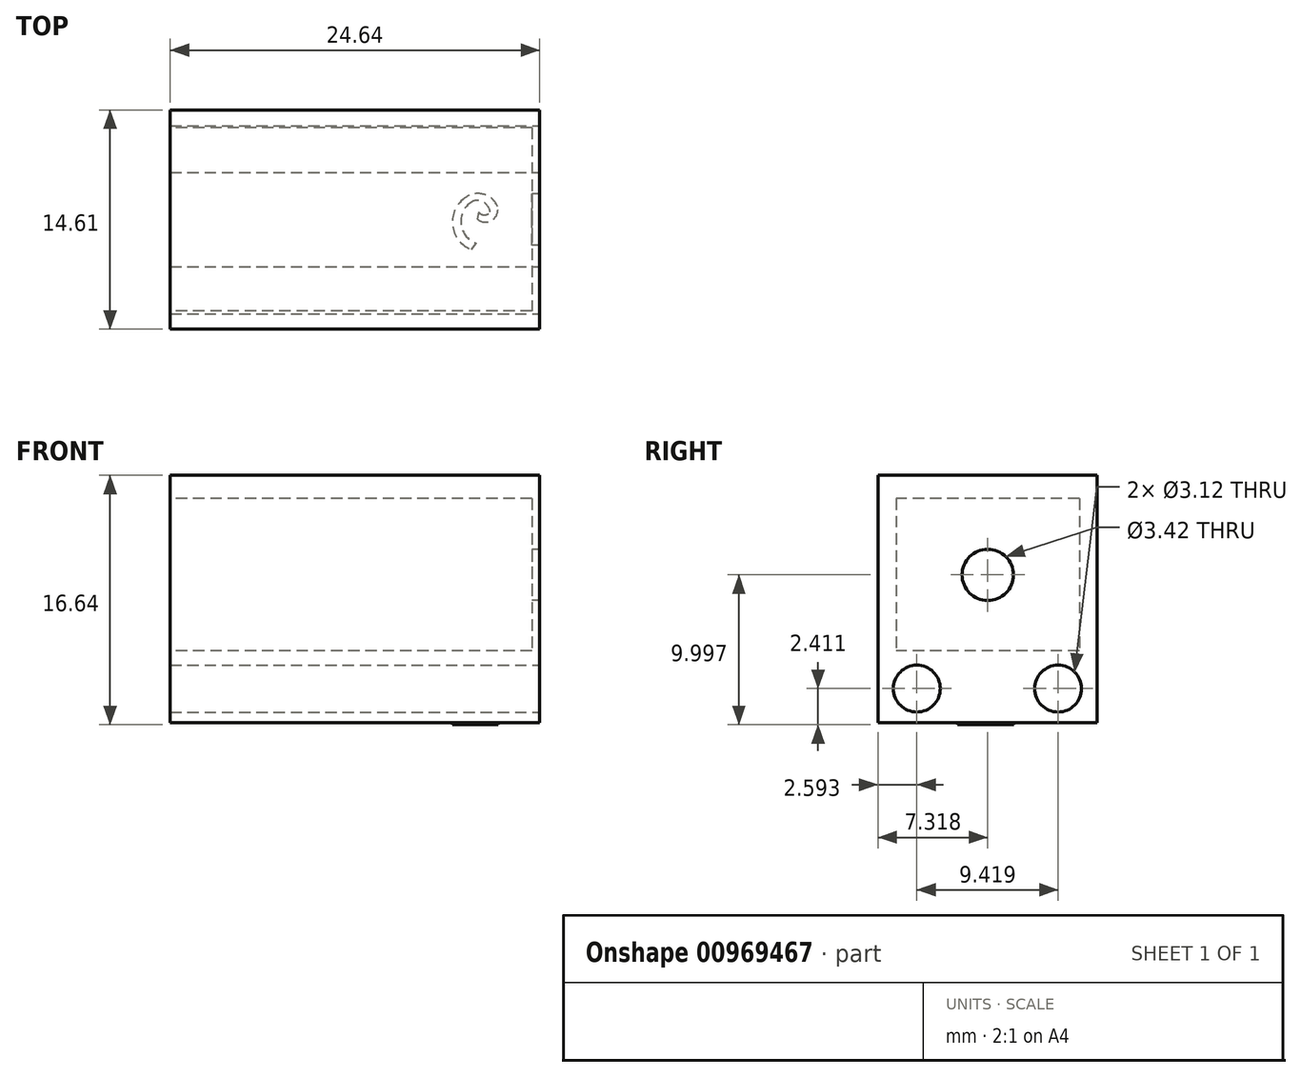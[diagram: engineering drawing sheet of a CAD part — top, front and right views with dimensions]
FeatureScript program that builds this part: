
annotation { "Feature Type Name" : "Feature", "Feature Type Description" : "" }
export const myFeature = defineFeature(function(context is Context, id is Id, definition is map)
    precondition{}
    {
        {
            var Q0;
            Q0=qCreatedBy(makeId("Front.planeOp"),FACE);
            var sketch = newSketch(context, id + "F0", { "sketchPlane" : qUnion([Q0])});
            skLineSegment(sketch, "E0.bottom", {"start": v(-13.1, 13.65) * mm, "end": v(11.55, 13.65) * mm});
            skLineSegment(sketch, "E0.top", {"start": v(-13.1, -2.86) * mm, "end": v(11.55, -2.86) * mm});
            skLineSegment(sketch, "E0.left", {"start": v(-13.1, 13.65) * mm, "end": v(-13.1, -2.86) * mm});
            skLineSegment(sketch, "E0.right", {"start": v(11.55, 13.65) * mm, "end": v(11.55, -2.86) * mm});
            skSolve(sketch);
        }
        {
            var Q0;
            Q0=makeQuery(id+"F0.imprint","IMPRINT",FACE,{"disambiguationData":[TD([[makeQuery(id+"F0.imprint","IMPRINT",EDGE,{"derivedFrom":sQuery(id+"F0.wireOp",EDGE,"E0.bottom")}),-1.0]])]});
            extrude(context, id + "F1", {"entities" : qUnion([Q0]), "depth" : 14.6 * mm, "offsetDistance" : 25.4 * mm});
        }
        {
            var Q0;
            Q0=makeQuery(id+"F1.opExtrude","SWEPT_FACE",FACE,{"disambiguationData":[OSD([sQuery(id+"F0.wireOp",EDGE,"E0.left")])]});
            var sketch = newSketch(context, id + "F2", { "sketchPlane" : qUnion([Q0])});
            skLineSegment(sketch, "E1.bottom", {"start": v(1.19, 12.09) * mm, "end": v(13.4, 12.09) * mm});
            skLineSegment(sketch, "E1.top", {"start": v(1.19, 1.93) * mm, "end": v(13.4, 1.93) * mm});
            skLineSegment(sketch, "E1.left", {"start": v(1.19, 12.09) * mm, "end": v(1.19, 1.93) * mm});
            skLineSegment(sketch, "E1.right", {"start": v(13.4, 12.09) * mm, "end": v(13.4, 1.93) * mm});
            skSolve(sketch);
        }
        {
            var Q0;
            Q0 = qSketchRegion(id + "F2", true);
            extrude(context, id + "F3", {"entities" : qUnion([Q0]), "operationType" : NewBodyOperationType.REMOVE, "oppositeDirection" : true, "depth" : 24.13 * mm, "offsetDistance" : 25.4 * mm});
        }
        {
            var Q0;
            Q0=makeQuery(id+"F3.boolean.opBoolean","COPY",FACE,{"derivedFrom":makeQuery(id+"F3.opExtrude","CAP_FACE",FACE,{"disambiguationData":[OSD([sQuery(id+"F2.wireOp",EDGE,"E1.bottom"),sQuery(id+"F2.wireOp",EDGE,"E1.top"),sQuery(id+"F2.wireOp",EDGE,"E1.left"),sQuery(id+"F2.wireOp",EDGE,"E1.right")])],"isStart":false})});
            var sketch = newSketch(context, id + "F4", { "sketchPlane" : qUnion([Q0])});
            skLineSegment(sketch, "E2", {"start": v(7.3, 12.09) * mm, "end": v(7.3, 1.93) * mm, "construction": true});
            skCircle(sketch, "E3", {"center": v(7.3, 7) * mm, "radius": 1.71 * mm});
            skSolve(sketch);
        }
        {
            var Q0;
            Q0 = qSketchRegion(id + "F4", true);
            extrude(context, id + "F5", {"entities" : qUnion([Q0]), "operationType" : NewBodyOperationType.REMOVE, "oppositeDirection" : true, "depth" : 25.4 * mm, "offsetDistance" : 25.4 * mm});
        }
        {
            var Q0;
            Q0=makeQuery(id+"F1.opExtrude","SWEPT_FACE",FACE,{"disambiguationData":[OSD([sQuery(id+"F0.wireOp",EDGE,"E0.right")])]});
            var sketch = newSketch(context, id + "F6", { "sketchPlane" : qUnion([Q0])});
            skCircle(sketch, "E4", {"center": v(-2.6, -0.58) * mm, "radius": 1.56 * mm});
            skCircle(sketch, "E5", {"center": v(-12.02, -0.58) * mm, "radius": 1.56 * mm});
            skSolve(sketch);
        }
        {
            var Q0;
            Q0 = qSketchRegion(id + "F6", true);
            extrude(context, id + "F7", {"entities" : qUnion([Q0]), "operationType" : NewBodyOperationType.REMOVE, "oppositeDirection" : true, "depth" : 25.4 * mm, "offsetDistance" : 25.4 * mm});
        }
        {
            var Q0;
            Q0=makeQuery(id+"F1.opExtrude","SWEPT_FACE",FACE,{"disambiguationData":[OSD([sQuery(id+"F0.wireOp",EDGE,"E0.top")])]});
            var sketch = newSketch(context, id + "F8", { "sketchPlane" : qUnion([Q0])});
            skArc(sketch, "E6", {"start": v(7, 9.3) * mm, "mid": v(5.74, 7.66) * mm, "end": v(6.64, 5.8) * mm});
            skArc(sketch, "E7", {"start": v(7.3, 8.88) * mm, "mid": v(6.3, 7.53) * mm, "end": v(7.13, 6.07) * mm});
            skArc(sketch, "E8", {"start": v(7.13, 6.07) * mm, "mid": v(7.85, 6.18) * mm, "end": v(8.24, 6.8) * mm});
            skArc(sketch, "E9", {"start": v(6.64, 5.8) * mm, "mid": v(7.85, 5.63) * mm, "end": v(8.75, 6.45) * mm});
            skArc(sketch, "E10", {"start": v(8.75, 6.45) * mm, "mid": v(8.37, 7.35) * mm, "end": v(7.4, 7.28) * mm});
            skArc(sketch, "E11", {"start": v(8.24, 6.8) * mm, "mid": v(7.86, 7) * mm, "end": v(7.48, 6.8) * mm});
            skLineSegment(sketch, "E12", {"start": v(7.48, 6.8) * mm, "end": v(7.4, 7.28) * mm});
            skLineSegment(sketch, "E13", {"start": v(7, 9.3) * mm, "end": v(7.3, 8.88) * mm});
            skSolve(sketch);
        }
        {
            var Q0;
            Q0 = qSketchRegion(id + "F8", true);
            extrude(context, id + "F9", {"entities" : qUnion([Q0]), "operationType" : NewBodyOperationType.ADD, "depth" : 0.13 * mm, "offsetDistance" : 25.4 * mm});
        }
    });
